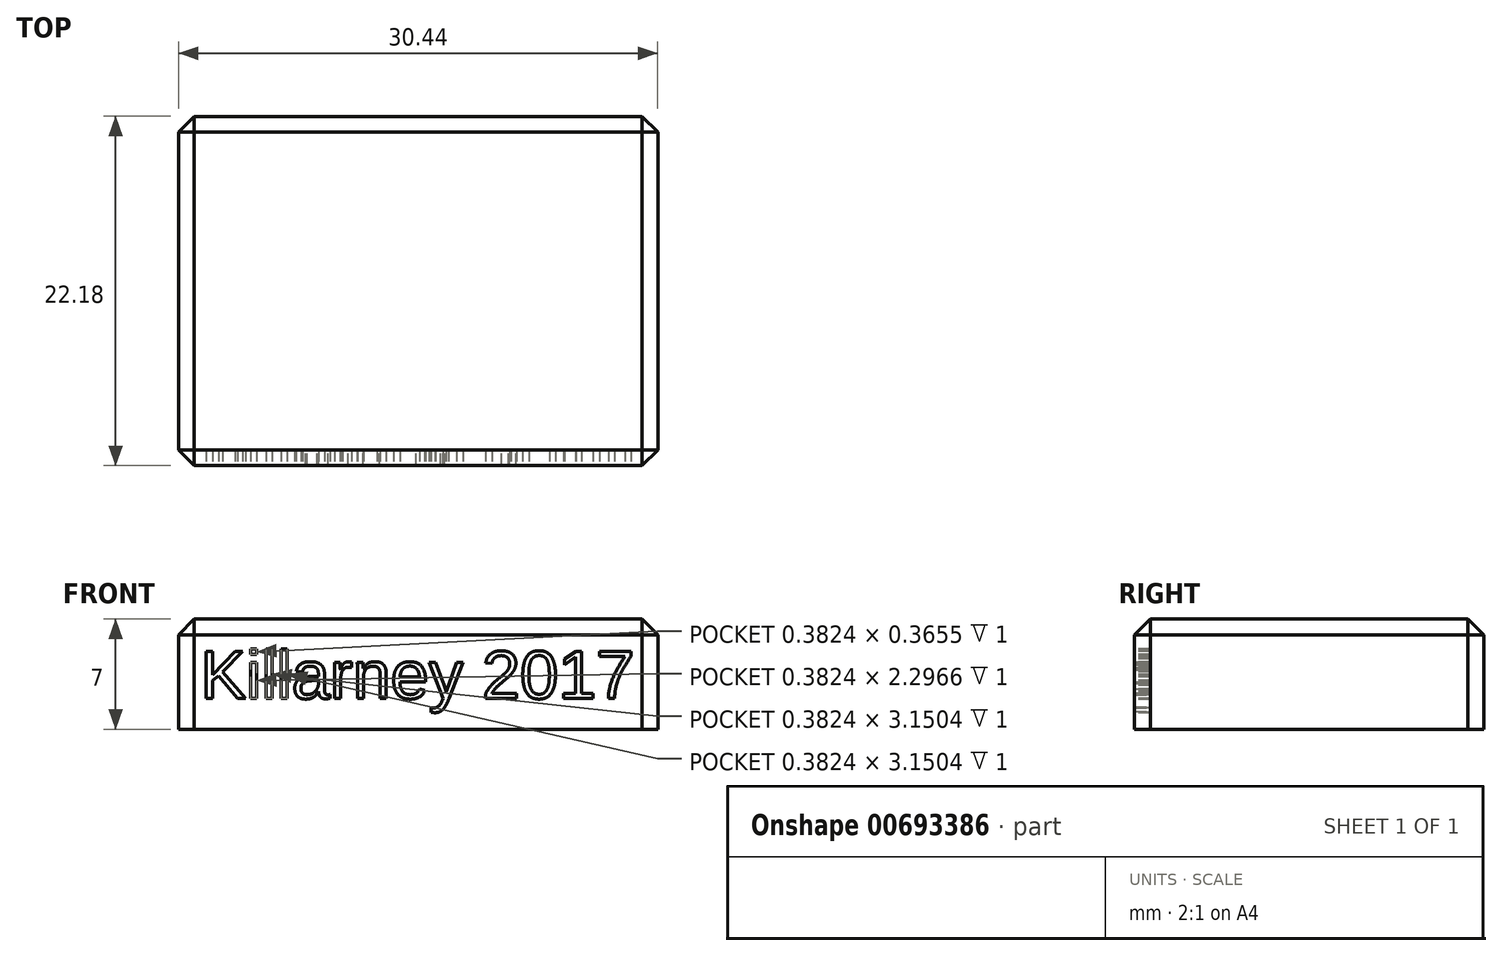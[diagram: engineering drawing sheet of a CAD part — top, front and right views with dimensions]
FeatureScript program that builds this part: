
annotation { "Feature Type Name" : "Feature", "Feature Type Description" : "" }
export const myFeature = defineFeature(function(context is Context, id is Id, definition is map)
    precondition{}
    {
        {
            var Q0;
            Q0=qCreatedBy(makeId("Top.planeOp"),FACE);
            var sketch = newSketch(context, id + "F0", { "sketchPlane" : qUnion([Q0])});
            skLineSegment(sketch, "E0.bottom", {"start": v(-15.22, 11.28) * mm, "end": v(15.22, 11.28) * mm});
            skLineSegment(sketch, "E0.top", {"start": v(-15.22, -10.9) * mm, "end": v(15.22, -10.9) * mm});
            skLineSegment(sketch, "E0.left", {"start": v(-15.22, 11.28) * mm, "end": v(-15.22, -10.9) * mm});
            skLineSegment(sketch, "E0.right", {"start": v(15.22, 11.28) * mm, "end": v(15.22, -10.9) * mm});
            skSolve(sketch);
        }
        {
            var Q0;
            Q0 = qSketchRegion(id + "F0", true);
            extrude(context, id + "F1", {"entities" : qUnion([Q0]), "depth" : 7 * mm, "offsetDistance" : 25 * mm});
        }
        {
            var Q0;
            Q0=makeQuery(id+"F1.opExtrude","SWEPT_FACE",FACE,{"disambiguationData":[OSD([sQuery(id+"F0.wireOp",EDGE,"E0.top")])]});
            var sketch = newSketch(context, id + "F2", { "sketchPlane" : qUnion([Q0])});
            skText(sketch, "E1", { "text": "Killarney 2017", "fontName": "Arimo-Regular.ttf"});
            const initialGuessF2  = {"E1": [-0.01382, 0.00195, 1, 0, 0.00313]};
            skSetInitialGuess(sketch, initialGuessF2);
            skSolve(sketch);
        }
        {
            var Q0;
            Q0 = qSketchRegion(id + "F2", true);
            extrude(context, id + "F3", {"entities" : qUnion([Q0]), "operationType" : NewBodyOperationType.REMOVE, "oppositeDirection" : true, "depth" : 1 * mm, "offsetDistance" : 25 * mm});
        }
        {
            var Q0;
            Q0=makeQuery(id+"F1.opExtrude","CAP_EDGE",EDGE,{"disambiguationData":[OSD([sQuery(id+"F0.wireOp",EDGE,"E0.bottom")])],"isStart":false});
            var Q1;
            Q1=makeQuery(id+"F1.opExtrude","CAP_EDGE",EDGE,{"disambiguationData":[OSD([sQuery(id+"F0.wireOp",EDGE,"E0.left")])],"isStart":false});
            var Q2;
            Q2=makeQuery(id+"F1.opExtrude","CAP_FACE",FACE,{"disambiguationData":[OSD([sQuery(id+"F0.wireOp",EDGE,"E0.bottom"),sQuery(id+"F0.wireOp",EDGE,"E0.top"),sQuery(id+"F0.wireOp",EDGE,"E0.left"),sQuery(id+"F0.wireOp",EDGE,"E0.right")])],"isStart":false});
            var Q3;
            Q3=makeQuery(id+"F1.opExtrude","SWEPT_EDGE",EDGE,{"disambiguationData":[OSD([sQuery(id+"F0.wireOp",EDGE,"E0.top"),sQuery(id+"F0.wireOp",EDGE,"E0.right")])]});
            var Q4;
            Q4=makeQuery(id+"F1.opExtrude","SWEPT_EDGE",EDGE,{"disambiguationData":[OSD([sQuery(id+"F0.wireOp",EDGE,"E0.top"),sQuery(id+"F0.wireOp",EDGE,"E0.left")])]});
            var Q5;
            Q5=makeQuery(id+"F1.opExtrude","SWEPT_EDGE",EDGE,{"disambiguationData":[OSD([sQuery(id+"F0.wireOp",EDGE,"E0.bottom"),sQuery(id+"F0.wireOp",EDGE,"E0.right")])]});
            var Q6;
            Q6=makeQuery(id+"F1.opExtrude","SWEPT_EDGE",EDGE,{"disambiguationData":[OSD([sQuery(id+"F0.wireOp",EDGE,"E0.bottom"),sQuery(id+"F0.wireOp",EDGE,"E0.left")])]});
            chamfer(context, id + "F4", {"entities" : qUnion([Q0, Q1, Q2, Q3, Q4, Q5, Q6]), "width" : 1 * mm, "tangentPropagation" : true});
        }
    });
